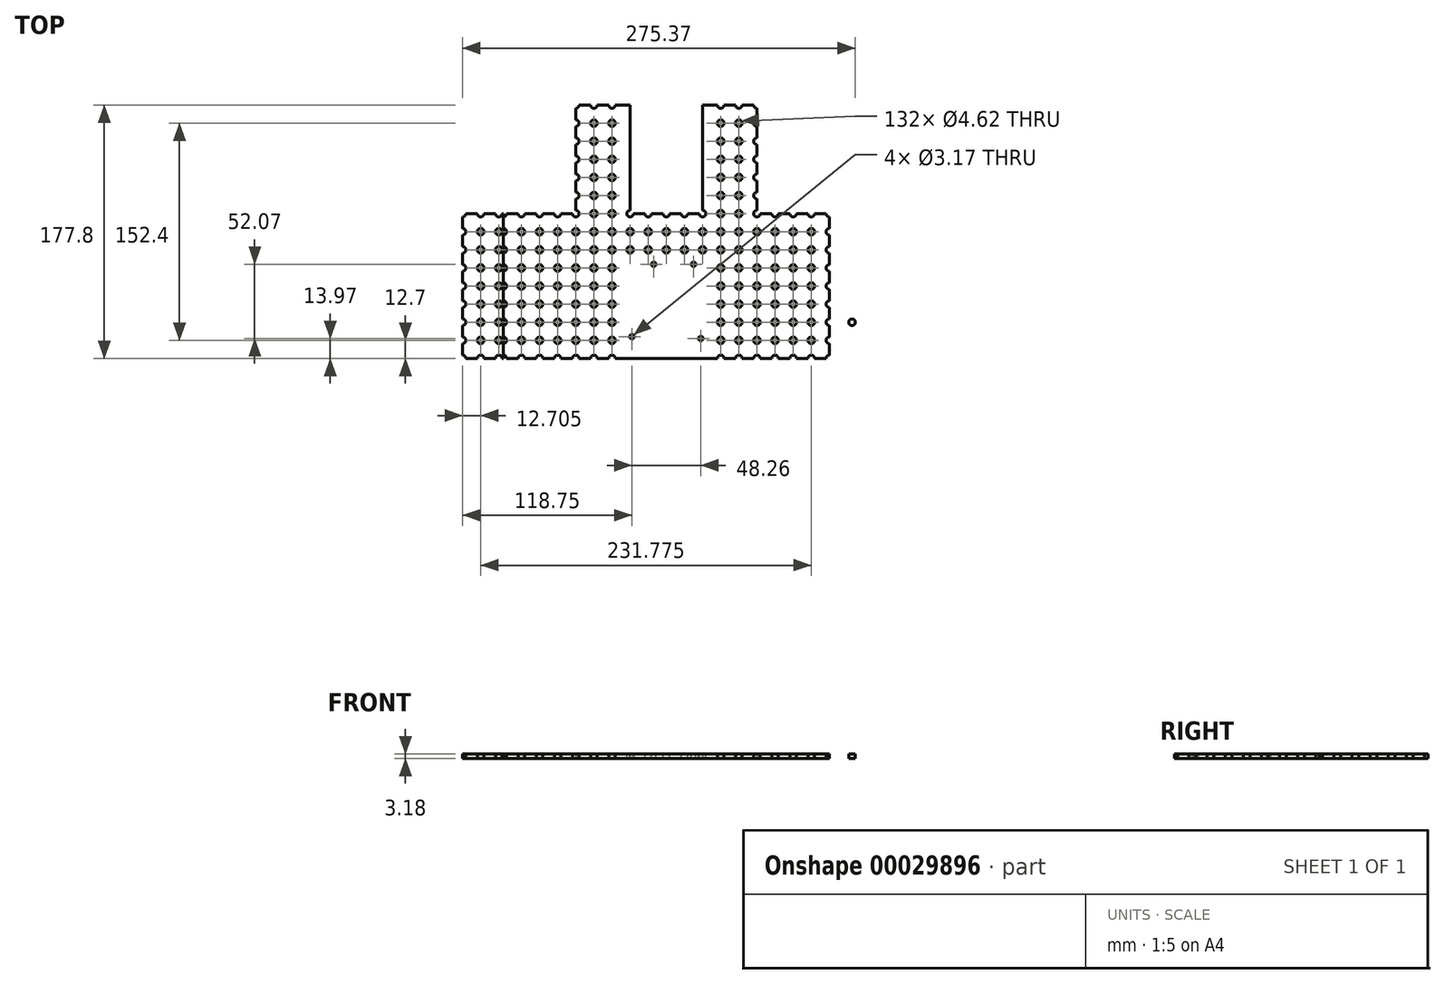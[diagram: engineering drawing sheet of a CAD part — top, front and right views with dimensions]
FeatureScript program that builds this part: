
annotation { "Feature Type Name" : "Feature", "Feature Type Description" : "" }
export const myFeature = defineFeature(function(context is Context, id is Id, definition is map)
    precondition{}
    {
        {
            var Q0;
            Q0=qCreatedBy(makeId("Top.planeOp"),FACE);
            var sketch = newSketch(context, id + "F0", { "sketchPlane" : qUnion([Q0])});
            skLineSegment(sketch, "E0", {"start": v(0, 0) * mm, "end": v(25.4, 0) * mm});
            skLineSegment(sketch, "E1", {"start": v(25.4, 0) * mm, "end": v(25.4, 76.2) * mm});
            skLineSegment(sketch, "E2", {"start": v(25.4, 76.2) * mm, "end": v(63.5, 76.2) * mm});
            skLineSegment(sketch, "E3", {"start": v(63.5, 76.2) * mm, "end": v(63.5, 0) * mm});
            skLineSegment(sketch, "E4", {"start": v(63.5, 0) * mm, "end": v(114.3, 0) * mm});
            skLineSegment(sketch, "E5", {"start": v(114.3, 0) * mm, "end": v(114.3, -101.6) * mm});
            skLineSegment(sketch, "E6", {"start": v(114.3, -101.6) * mm, "end": v(0, -101.6) * mm});
            skLineSegment(sketch, "E7", {"start": v(0, 0) * mm, "end": v(0, -101.6) * mm, "construction": true});
            skLineSegment(sketch, "E8.MirrorCS", {"start": v(0, 0) * mm, "end": v(-25.4, 0) * mm});
            skLineSegment(sketch, "E9.MirrorCS", {"start": v(-25.4, 0) * mm, "end": v(-25.4, 76.2) * mm});
            skLineSegment(sketch, "E10.MirrorCS", {"start": v(-114.3, 0) * mm, "end": v(-114.3, -101.6) * mm});
            skLineSegment(sketch, "E11.MirrorCS", {"start": v(-25.4, 76.2) * mm, "end": v(-63.5, 76.2) * mm});
            skLineSegment(sketch, "E12.MirrorCS", {"start": v(-63.5, 0) * mm, "end": v(-114.3, 0) * mm});
            skLineSegment(sketch, "E13.MirrorCS", {"start": v(-114.3, -101.6) * mm, "end": v(0, -101.6) * mm});
            skLineSegment(sketch, "E14.MirrorCS", {"start": v(-63.5, 76.2) * mm, "end": v(-63.5, 0) * mm});
            skSolve(sketch);
        }
        {
            var Q0;
            Q0=makeQuery(id+"F0.imprint","IMPRINT",FACE,{"disambiguationData":[TD([[makeQuery(id+"F0.imprint","IMPRINT",EDGE,{"derivedFrom":sQuery(id+"F0.wireOp",EDGE,"E0")}),-1.0]])]});
            extrude(context, id + "F1", {"entities" : qUnion([Q0]), "depth" : 3.17 * mm});
        }
        {
            var Q0;
            Q0=qCreatedBy(makeId("Top.planeOp"),FACE);
            var sketch = newSketch(context, id + "F2", { "sketchPlane" : qUnion([Q0])});
            skPoint(sketch, "E15.0", {"position": v(114.3, -101.6) * mm});
            skCircle(sketch, "E16", {"center": v(114.3, -101.6) * mm, "radius": 2.31 * mm});
            skCircle(sketch, "E17.0.1.0", {"center": v(114.3, -88.9) * mm, "radius": 2.31 * mm});
            skCircle(sketch, "E17.0.2.0", {"center": v(114.3, -76.2) * mm, "radius": 2.31 * mm});
            skCircle(sketch, "E17.0.3.0", {"center": v(114.3, -63.5) * mm, "radius": 2.31 * mm});
            skCircle(sketch, "E17.0.4.0", {"center": v(114.3, -50.8) * mm, "radius": 2.31 * mm});
            skCircle(sketch, "E17.0.5.0", {"center": v(114.3, -38.1) * mm, "radius": 2.31 * mm});
            skCircle(sketch, "E17.0.6.0", {"center": v(114.3, -25.4) * mm, "radius": 2.31 * mm});
            skCircle(sketch, "E17.0.7.0", {"center": v(114.3, -12.7) * mm, "radius": 2.31 * mm});
            skCircle(sketch, "E17.0.8.0", {"center": v(114.3, 0) * mm, "radius": 2.31 * mm});
            skCircle(sketch, "E17.0.9.0", {"center": v(114.3, 12.7) * mm, "radius": 2.31 * mm});
            skCircle(sketch, "E17.0.10.0", {"center": v(114.3, 25.4) * mm, "radius": 2.31 * mm});
            skCircle(sketch, "E17.0.11.0", {"center": v(114.3, 38.1) * mm, "radius": 2.31 * mm});
            skCircle(sketch, "E17.0.12.0", {"center": v(114.3, 50.8) * mm, "radius": 2.31 * mm});
            skCircle(sketch, "E17.0.13.0", {"center": v(114.3, 63.5) * mm, "radius": 2.31 * mm});
            skCircle(sketch, "E17.0.14.0", {"center": v(114.3, 76.2) * mm, "radius": 2.31 * mm});
            skCircle(sketch, "E17.1.0.0", {"center": v(101.6, -101.6) * mm, "radius": 2.31 * mm});
            skCircle(sketch, "E17.1.1.0", {"center": v(101.6, -88.9) * mm, "radius": 2.31 * mm});
            skCircle(sketch, "E17.1.2.0", {"center": v(101.6, -76.2) * mm, "radius": 2.31 * mm});
            skCircle(sketch, "E17.1.3.0", {"center": v(101.6, -63.5) * mm, "radius": 2.31 * mm});
            skCircle(sketch, "E17.1.4.0", {"center": v(101.6, -50.8) * mm, "radius": 2.31 * mm});
            skCircle(sketch, "E17.1.5.0", {"center": v(101.6, -38.1) * mm, "radius": 2.31 * mm});
            skCircle(sketch, "E17.1.6.0", {"center": v(101.6, -25.4) * mm, "radius": 2.31 * mm});
            skCircle(sketch, "E17.1.7.0", {"center": v(101.6, -12.7) * mm, "radius": 2.31 * mm});
            skCircle(sketch, "E17.1.8.0", {"center": v(101.6, 0) * mm, "radius": 2.31 * mm});
            skCircle(sketch, "E17.1.9.0", {"center": v(101.6, 12.7) * mm, "radius": 2.31 * mm});
            skCircle(sketch, "E17.1.10.0", {"center": v(101.6, 25.4) * mm, "radius": 2.31 * mm});
            skCircle(sketch, "E17.1.11.0", {"center": v(101.6, 38.1) * mm, "radius": 2.31 * mm});
            skCircle(sketch, "E17.1.12.0", {"center": v(101.6, 50.8) * mm, "radius": 2.31 * mm});
            skCircle(sketch, "E17.1.13.0", {"center": v(101.6, 63.5) * mm, "radius": 2.31 * mm});
            skCircle(sketch, "E17.1.14.0", {"center": v(101.6, 76.2) * mm, "radius": 2.31 * mm});
            skCircle(sketch, "E17.2.0.0", {"center": v(88.9, -101.6) * mm, "radius": 2.31 * mm});
            skCircle(sketch, "E17.2.1.0", {"center": v(88.9, -88.9) * mm, "radius": 2.31 * mm});
            skCircle(sketch, "E17.2.2.0", {"center": v(88.9, -76.2) * mm, "radius": 2.31 * mm});
            skCircle(sketch, "E17.2.3.0", {"center": v(88.9, -63.5) * mm, "radius": 2.31 * mm});
            skCircle(sketch, "E17.2.4.0", {"center": v(88.9, -50.8) * mm, "radius": 2.31 * mm});
            skCircle(sketch, "E17.2.5.0", {"center": v(88.9, -38.1) * mm, "radius": 2.31 * mm});
            skCircle(sketch, "E17.2.6.0", {"center": v(88.9, -25.4) * mm, "radius": 2.31 * mm});
            skCircle(sketch, "E17.2.7.0", {"center": v(88.9, -12.7) * mm, "radius": 2.31 * mm});
            skCircle(sketch, "E17.2.8.0", {"center": v(88.9, 0) * mm, "radius": 2.31 * mm});
            skCircle(sketch, "E17.2.9.0", {"center": v(88.9, 12.7) * mm, "radius": 2.31 * mm});
            skCircle(sketch, "E17.2.10.0", {"center": v(88.9, 25.4) * mm, "radius": 2.31 * mm});
            skCircle(sketch, "E17.2.11.0", {"center": v(88.9, 38.1) * mm, "radius": 2.31 * mm});
            skCircle(sketch, "E17.2.12.0", {"center": v(88.9, 50.8) * mm, "radius": 2.31 * mm});
            skCircle(sketch, "E17.2.13.0", {"center": v(88.9, 63.5) * mm, "radius": 2.31 * mm});
            skCircle(sketch, "E17.2.14.0", {"center": v(88.9, 76.2) * mm, "radius": 2.31 * mm});
            skCircle(sketch, "E17.3.0.0", {"center": v(76.2, -101.6) * mm, "radius": 2.31 * mm});
            skCircle(sketch, "E17.3.1.0", {"center": v(76.2, -88.9) * mm, "radius": 2.31 * mm});
            skCircle(sketch, "E17.3.2.0", {"center": v(76.2, -76.2) * mm, "radius": 2.31 * mm});
            skCircle(sketch, "E17.3.3.0", {"center": v(76.2, -63.5) * mm, "radius": 2.31 * mm});
            skCircle(sketch, "E17.3.4.0", {"center": v(76.2, -50.8) * mm, "radius": 2.31 * mm});
            skCircle(sketch, "E17.3.5.0", {"center": v(76.2, -38.1) * mm, "radius": 2.31 * mm});
            skCircle(sketch, "E17.3.6.0", {"center": v(76.2, -25.4) * mm, "radius": 2.31 * mm});
            skCircle(sketch, "E17.3.7.0", {"center": v(76.2, -12.7) * mm, "radius": 2.31 * mm});
            skCircle(sketch, "E17.3.8.0", {"center": v(76.2, 0) * mm, "radius": 2.31 * mm});
            skCircle(sketch, "E17.3.9.0", {"center": v(76.2, 12.7) * mm, "radius": 2.31 * mm});
            skCircle(sketch, "E17.3.10.0", {"center": v(76.2, 25.4) * mm, "radius": 2.31 * mm});
            skCircle(sketch, "E17.3.11.0", {"center": v(76.2, 38.1) * mm, "radius": 2.31 * mm});
            skCircle(sketch, "E17.3.12.0", {"center": v(76.2, 50.8) * mm, "radius": 2.31 * mm});
            skCircle(sketch, "E17.3.13.0", {"center": v(76.2, 63.5) * mm, "radius": 2.31 * mm});
            skCircle(sketch, "E17.3.14.0", {"center": v(76.2, 76.2) * mm, "radius": 2.31 * mm});
            skCircle(sketch, "E17.4.0.0", {"center": v(63.5, -101.6) * mm, "radius": 2.31 * mm});
            skCircle(sketch, "E17.4.1.0", {"center": v(63.5, -88.9) * mm, "radius": 2.31 * mm});
            skCircle(sketch, "E17.4.2.0", {"center": v(63.5, -76.2) * mm, "radius": 2.31 * mm});
            skCircle(sketch, "E17.4.3.0", {"center": v(63.5, -63.5) * mm, "radius": 2.31 * mm});
            skCircle(sketch, "E17.4.4.0", {"center": v(63.5, -50.8) * mm, "radius": 2.31 * mm});
            skCircle(sketch, "E17.4.5.0", {"center": v(63.5, -38.1) * mm, "radius": 2.31 * mm});
            skCircle(sketch, "E17.4.6.0", {"center": v(63.5, -25.4) * mm, "radius": 2.31 * mm});
            skCircle(sketch, "E17.4.7.0", {"center": v(63.5, -12.7) * mm, "radius": 2.31 * mm});
            skCircle(sketch, "E17.4.8.0", {"center": v(63.5, 0) * mm, "radius": 2.31 * mm});
            skCircle(sketch, "E17.4.9.0", {"center": v(63.5, 12.7) * mm, "radius": 2.31 * mm});
            skCircle(sketch, "E17.4.10.0", {"center": v(63.5, 25.4) * mm, "radius": 2.31 * mm});
            skCircle(sketch, "E17.4.11.0", {"center": v(63.5, 38.1) * mm, "radius": 2.31 * mm});
            skCircle(sketch, "E17.4.12.0", {"center": v(63.5, 50.8) * mm, "radius": 2.31 * mm});
            skCircle(sketch, "E17.4.13.0", {"center": v(63.5, 63.5) * mm, "radius": 2.31 * mm});
            skCircle(sketch, "E17.4.14.0", {"center": v(63.5, 76.2) * mm, "radius": 2.31 * mm});
            skLineSegment(sketch, "E17.direction1", {"start": v(114.3, -101.6) * mm, "end": v(101.6, -101.6) * mm, "construction": true});
            skLineSegment(sketch, "E17.direction2", {"start": v(114.3, -101.6) * mm, "end": v(114.3, -88.9) * mm, "construction": true});
            skLineSegment(sketch, "E18", {"start": v(0, 0) * mm, "end": v(0, -13.36) * mm, "construction": true});
            skCircle(sketch, "E19.0.5.0", {"center": v(50.8, -101.6) * mm, "radius": 2.31 * mm});
            skCircle(sketch, "E19.0.5.1", {"center": v(50.8, -88.9) * mm, "radius": 2.31 * mm});
            skCircle(sketch, "E19.0.5.2", {"center": v(50.8, -76.2) * mm, "radius": 2.31 * mm});
            skCircle(sketch, "E19.0.5.3", {"center": v(50.8, -63.5) * mm, "radius": 2.31 * mm});
            skCircle(sketch, "E19.0.5.4", {"center": v(50.8, -50.8) * mm, "radius": 2.31 * mm});
            skCircle(sketch, "E19.0.5.5", {"center": v(50.8, -38.1) * mm, "radius": 2.31 * mm});
            skCircle(sketch, "E19.0.5.6", {"center": v(50.8, -25.4) * mm, "radius": 2.31 * mm});
            skCircle(sketch, "E19.0.5.7", {"center": v(50.8, -12.7) * mm, "radius": 2.31 * mm});
            skCircle(sketch, "E19.0.5.8", {"center": v(50.8, 0) * mm, "radius": 2.31 * mm});
            skCircle(sketch, "E19.0.5.9", {"center": v(50.8, 12.7) * mm, "radius": 2.31 * mm});
            skCircle(sketch, "E19.0.5.10", {"center": v(50.8, 25.4) * mm, "radius": 2.31 * mm});
            skCircle(sketch, "E19.0.5.11", {"center": v(50.8, 38.1) * mm, "radius": 2.31 * mm});
            skCircle(sketch, "E19.0.5.12", {"center": v(50.8, 50.8) * mm, "radius": 2.31 * mm});
            skCircle(sketch, "E19.0.5.13", {"center": v(50.8, 63.5) * mm, "radius": 2.31 * mm});
            skCircle(sketch, "E19.0.5.14", {"center": v(50.8, 76.2) * mm, "radius": 2.31 * mm});
            skCircle(sketch, "E19.0.6.0", {"center": v(38.1, -101.6) * mm, "radius": 2.31 * mm});
            skCircle(sketch, "E19.0.6.1", {"center": v(38.1, -88.9) * mm, "radius": 2.31 * mm});
            skCircle(sketch, "E19.0.6.2", {"center": v(38.1, -76.2) * mm, "radius": 2.31 * mm});
            skCircle(sketch, "E19.0.6.3", {"center": v(38.1, -63.5) * mm, "radius": 2.31 * mm});
            skCircle(sketch, "E19.0.6.4", {"center": v(38.1, -50.8) * mm, "radius": 2.31 * mm});
            skCircle(sketch, "E19.0.6.5", {"center": v(38.1, -38.1) * mm, "radius": 2.31 * mm});
            skCircle(sketch, "E19.0.6.6", {"center": v(38.1, -25.4) * mm, "radius": 2.31 * mm});
            skCircle(sketch, "E19.0.6.7", {"center": v(38.1, -12.7) * mm, "radius": 2.31 * mm});
            skCircle(sketch, "E19.0.6.8", {"center": v(38.1, 0) * mm, "radius": 2.31 * mm});
            skCircle(sketch, "E19.0.6.9", {"center": v(38.1, 12.7) * mm, "radius": 2.31 * mm});
            skCircle(sketch, "E19.0.6.10", {"center": v(38.1, 25.4) * mm, "radius": 2.31 * mm});
            skCircle(sketch, "E19.0.6.11", {"center": v(38.1, 38.1) * mm, "radius": 2.31 * mm});
            skCircle(sketch, "E19.0.6.12", {"center": v(38.1, 50.8) * mm, "radius": 2.31 * mm});
            skCircle(sketch, "E19.0.6.13", {"center": v(38.1, 63.5) * mm, "radius": 2.31 * mm});
            skCircle(sketch, "E19.0.6.14", {"center": v(38.1, 76.2) * mm, "radius": 2.31 * mm});
            skCircle(sketch, "E20.MirrorC", {"center": v(-114.3, -101.6) * mm, "radius": 2.31 * mm});
            skCircle(sketch, "E21.MirrorC", {"center": v(-101.6, -76.2) * mm, "radius": 2.31 * mm});
            skCircle(sketch, "E22.MirrorC", {"center": v(-101.6, -88.9) * mm, "radius": 2.31 * mm});
            skCircle(sketch, "E23.MirrorC", {"center": v(-114.3, -88.9) * mm, "radius": 2.31 * mm});
            skCircle(sketch, "E24.MirrorC", {"center": v(-101.6, -101.6) * mm, "radius": 2.31 * mm});
            skLineSegment(sketch, "E25.MirrorCS", {"start": v(-114.3, -101.6) * mm, "end": v(-101.6, -101.6) * mm});
            skCircle(sketch, "E26.MirrorC", {"center": v(-88.9, -88.9) * mm, "radius": 2.31 * mm});
            skCircle(sketch, "E27.MirrorC", {"center": v(-76.2, -12.7) * mm, "radius": 2.31 * mm});
            skCircle(sketch, "E28.MirrorC", {"center": v(-63.5, 0) * mm, "radius": 2.31 * mm});
            skCircle(sketch, "E29.MirrorC", {"center": v(-50.8, -25.4) * mm, "radius": 2.31 * mm});
            skCircle(sketch, "E30.MirrorC", {"center": v(-38.1, -12.7) * mm, "radius": 2.31 * mm});
            skCircle(sketch, "E31.MirrorC", {"center": v(-101.6, -38.1) * mm, "radius": 2.31 * mm});
            skCircle(sketch, "E32.MirrorC", {"center": v(-88.9, -25.4) * mm, "radius": 2.31 * mm});
            skCircle(sketch, "E33.MirrorC", {"center": v(-114.3, 63.5) * mm, "radius": 2.31 * mm});
            skCircle(sketch, "E34.MirrorC", {"center": v(-76.2, -25.4) * mm, "radius": 2.31 * mm});
            skCircle(sketch, "E35.MirrorC", {"center": v(-63.5, -12.7) * mm, "radius": 2.31 * mm});
            skCircle(sketch, "E36.MirrorC", {"center": v(-50.8, -38.1) * mm, "radius": 2.31 * mm});
            skCircle(sketch, "E37.MirrorC", {"center": v(-38.1, -25.4) * mm, "radius": 2.31 * mm});
            skCircle(sketch, "E38.MirrorC", {"center": v(-101.6, -50.8) * mm, "radius": 2.31 * mm});
            skCircle(sketch, "E39.MirrorC", {"center": v(-88.9, -38.1) * mm, "radius": 2.31 * mm});
            skCircle(sketch, "E40.MirrorC", {"center": v(-101.6, -25.4) * mm, "radius": 2.31 * mm});
            skCircle(sketch, "E41.MirrorC", {"center": v(-88.9, -12.7) * mm, "radius": 2.31 * mm});
            skCircle(sketch, "E42.MirrorC", {"center": v(-76.2, -88.9) * mm, "radius": 2.31 * mm});
            skCircle(sketch, "E43.MirrorC", {"center": v(-76.2, -38.1) * mm, "radius": 2.31 * mm});
            skCircle(sketch, "E44.MirrorC", {"center": v(-50.8, 25.4) * mm, "radius": 2.31 * mm});
            skCircle(sketch, "E45.MirrorC", {"center": v(-63.5, -25.4) * mm, "radius": 2.31 * mm});
            skCircle(sketch, "E46.MirrorC", {"center": v(-50.8, -50.8) * mm, "radius": 2.31 * mm});
            skCircle(sketch, "E47.MirrorC", {"center": v(-38.1, -38.1) * mm, "radius": 2.31 * mm});
            skCircle(sketch, "E48.MirrorC", {"center": v(-63.5, -76.2) * mm, "radius": 2.31 * mm});
            skCircle(sketch, "E49.MirrorC", {"center": v(-101.6, -63.5) * mm, "radius": 2.31 * mm});
            skCircle(sketch, "E50.MirrorC", {"center": v(-38.1, 38.1) * mm, "radius": 2.31 * mm});
            skCircle(sketch, "E51.MirrorC", {"center": v(-88.9, -50.8) * mm, "radius": 2.31 * mm});
            skCircle(sketch, "E52.MirrorC", {"center": v(-101.6, 12.7) * mm, "radius": 2.31 * mm});
            skCircle(sketch, "E53.MirrorC", {"center": v(-88.9, 25.4) * mm, "radius": 2.31 * mm});
            skCircle(sketch, "E54.MirrorC", {"center": v(-76.2, 38.1) * mm, "radius": 2.31 * mm});
            skCircle(sketch, "E55.MirrorC", {"center": v(-63.5, 50.8) * mm, "radius": 2.31 * mm});
            skCircle(sketch, "E56.MirrorC", {"center": v(-76.2, -50.8) * mm, "radius": 2.31 * mm});
            skCircle(sketch, "E57.MirrorC", {"center": v(-63.5, -38.1) * mm, "radius": 2.31 * mm});
            skCircle(sketch, "E58.MirrorC", {"center": v(-50.8, 12.7) * mm, "radius": 2.31 * mm});
            skCircle(sketch, "E59.MirrorC", {"center": v(-50.8, -63.5) * mm, "radius": 2.31 * mm});
            skCircle(sketch, "E60.MirrorC", {"center": v(-38.1, -50.8) * mm, "radius": 2.31 * mm});
            skCircle(sketch, "E61.MirrorC", {"center": v(-38.1, 25.4) * mm, "radius": 2.31 * mm});
            skCircle(sketch, "E62.MirrorC", {"center": v(-38.1, 50.8) * mm, "radius": 2.31 * mm});
            skCircle(sketch, "E63.MirrorC", {"center": v(-88.9, -63.5) * mm, "radius": 2.31 * mm});
            skCircle(sketch, "E64.MirrorC", {"center": v(-101.6, 25.4) * mm, "radius": 2.31 * mm});
            skCircle(sketch, "E65.MirrorC", {"center": v(-50.8, -101.6) * mm, "radius": 2.31 * mm});
            skCircle(sketch, "E66.MirrorC", {"center": v(-38.1, -88.9) * mm, "radius": 2.31 * mm});
            skCircle(sketch, "E67.MirrorC", {"center": v(-114.3, 25.4) * mm, "radius": 2.31 * mm});
            skCircle(sketch, "E68.MirrorC", {"center": v(-114.3, 12.7) * mm, "radius": 2.31 * mm});
            skCircle(sketch, "E69.MirrorC", {"center": v(-114.3, 0) * mm, "radius": 2.31 * mm});
            skCircle(sketch, "E70.MirrorC", {"center": v(-114.3, -12.7) * mm, "radius": 2.31 * mm});
            skCircle(sketch, "E71.MirrorC", {"center": v(-88.9, -76.2) * mm, "radius": 2.31 * mm});
            skCircle(sketch, "E72.MirrorC", {"center": v(-114.3, -25.4) * mm, "radius": 2.31 * mm});
            skCircle(sketch, "E73.MirrorC", {"center": v(-114.3, -38.1) * mm, "radius": 2.31 * mm});
            skCircle(sketch, "E74.MirrorC", {"center": v(-114.3, -50.8) * mm, "radius": 2.31 * mm});
            skCircle(sketch, "E75.MirrorC", {"center": v(-114.3, -63.5) * mm, "radius": 2.31 * mm});
            skCircle(sketch, "E76.MirrorC", {"center": v(-114.3, -76.2) * mm, "radius": 2.31 * mm});
            skCircle(sketch, "E77.MirrorC", {"center": v(-76.2, -63.5) * mm, "radius": 2.31 * mm});
            skCircle(sketch, "E78.MirrorC", {"center": v(-63.5, -50.8) * mm, "radius": 2.31 * mm});
            skCircle(sketch, "E79.MirrorC", {"center": v(-50.8, -76.2) * mm, "radius": 2.31 * mm});
            skCircle(sketch, "E80.MirrorC", {"center": v(-114.3, 76.2) * mm, "radius": 2.31 * mm});
            skCircle(sketch, "E81.MirrorC", {"center": v(-38.1, -63.5) * mm, "radius": 2.31 * mm});
            skCircle(sketch, "E82.MirrorC", {"center": v(-101.6, 0) * mm, "radius": 2.31 * mm});
            skCircle(sketch, "E83.MirrorC", {"center": v(-76.2, 25.4) * mm, "radius": 2.31 * mm});
            skCircle(sketch, "E84.MirrorC", {"center": v(-88.9, 12.7) * mm, "radius": 2.31 * mm});
            skCircle(sketch, "E85.MirrorC", {"center": v(-88.9, -101.6) * mm, "radius": 2.31 * mm});
            skCircle(sketch, "E86.MirrorC", {"center": v(-50.8, 76.2) * mm, "radius": 2.31 * mm});
            skCircle(sketch, "E87.MirrorC", {"center": v(-101.6, 63.5) * mm, "radius": 2.31 * mm});
            skCircle(sketch, "E88.MirrorC", {"center": v(-88.9, 76.2) * mm, "radius": 2.31 * mm});
            skCircle(sketch, "E89.MirrorC", {"center": v(-63.5, -101.6) * mm, "radius": 2.31 * mm});
            skLineSegment(sketch, "E90.MirrorCS", {"start": v(-114.3, -101.6) * mm, "end": v(-114.3, -88.9) * mm});
            skCircle(sketch, "E91.MirrorC", {"center": v(-63.5, 38.1) * mm, "radius": 2.31 * mm});
            skCircle(sketch, "E92.MirrorC", {"center": v(-76.2, -101.6) * mm, "radius": 2.31 * mm});
            skCircle(sketch, "E93.MirrorC", {"center": v(-63.5, -88.9) * mm, "radius": 2.31 * mm});
            skCircle(sketch, "E94.MirrorC", {"center": v(-38.1, -101.6) * mm, "radius": 2.31 * mm});
            skCircle(sketch, "E95.MirrorC", {"center": v(-76.2, 12.7) * mm, "radius": 2.31 * mm});
            skCircle(sketch, "E96.MirrorC", {"center": v(-63.5, 25.4) * mm, "radius": 2.31 * mm});
            skCircle(sketch, "E97.MirrorC", {"center": v(-50.8, 0) * mm, "radius": 2.31 * mm});
            skCircle(sketch, "E98.MirrorC", {"center": v(-101.6, 76.2) * mm, "radius": 2.31 * mm});
            skCircle(sketch, "E99.MirrorC", {"center": v(-50.8, 63.5) * mm, "radius": 2.31 * mm});
            skCircle(sketch, "E100.MirrorC", {"center": v(-38.1, 12.7) * mm, "radius": 2.31 * mm});
            skCircle(sketch, "E101.MirrorC", {"center": v(-101.6, -12.7) * mm, "radius": 2.31 * mm});
            skCircle(sketch, "E102.MirrorC", {"center": v(-50.8, 50.8) * mm, "radius": 2.31 * mm});
            skCircle(sketch, "E103.MirrorC", {"center": v(-38.1, 63.5) * mm, "radius": 2.31 * mm});
            skCircle(sketch, "E104.MirrorC", {"center": v(-101.6, 38.1) * mm, "radius": 2.31 * mm});
            skCircle(sketch, "E105.MirrorC", {"center": v(-88.9, 50.8) * mm, "radius": 2.31 * mm});
            skCircle(sketch, "E106.MirrorC", {"center": v(-76.2, 63.5) * mm, "radius": 2.31 * mm});
            skCircle(sketch, "E107.MirrorC", {"center": v(-63.5, 76.2) * mm, "radius": 2.31 * mm});
            skCircle(sketch, "E108.MirrorC", {"center": v(-88.9, 0) * mm, "radius": 2.31 * mm});
            skCircle(sketch, "E109.MirrorC", {"center": v(-50.8, 38.1) * mm, "radius": 2.31 * mm});
            skCircle(sketch, "E110.MirrorC", {"center": v(-114.3, 50.8) * mm, "radius": 2.31 * mm});
            skCircle(sketch, "E111.MirrorC", {"center": v(-88.9, 38.1) * mm, "radius": 2.31 * mm});
            skCircle(sketch, "E112.MirrorC", {"center": v(-76.2, 50.8) * mm, "radius": 2.31 * mm});
            skCircle(sketch, "E113.MirrorC", {"center": v(-114.3, 38.1) * mm, "radius": 2.31 * mm});
            skCircle(sketch, "E114.MirrorC", {"center": v(-63.5, 63.5) * mm, "radius": 2.31 * mm});
            skCircle(sketch, "E115.MirrorC", {"center": v(-38.1, 76.2) * mm, "radius": 2.31 * mm});
            skCircle(sketch, "E116.MirrorC", {"center": v(-101.6, 50.8) * mm, "radius": 2.31 * mm});
            skCircle(sketch, "E117.MirrorC", {"center": v(-88.9, 63.5) * mm, "radius": 2.31 * mm});
            skCircle(sketch, "E118.MirrorC", {"center": v(-76.2, 76.2) * mm, "radius": 2.31 * mm});
            skCircle(sketch, "E119.MirrorC", {"center": v(-76.2, 0) * mm, "radius": 2.31 * mm});
            skCircle(sketch, "E120.MirrorC", {"center": v(-63.5, 12.7) * mm, "radius": 2.31 * mm});
            skCircle(sketch, "E121.MirrorC", {"center": v(-76.2, -76.2) * mm, "radius": 2.31 * mm});
            skCircle(sketch, "E122.MirrorC", {"center": v(-50.8, -12.7) * mm, "radius": 2.31 * mm});
            skCircle(sketch, "E123.MirrorC", {"center": v(-38.1, 0) * mm, "radius": 2.31 * mm});
            skCircle(sketch, "E124.MirrorC", {"center": v(-63.5, -63.5) * mm, "radius": 2.31 * mm});
            skCircle(sketch, "E125.MirrorC", {"center": v(-50.8, -88.9) * mm, "radius": 2.31 * mm});
            skCircle(sketch, "E126.MirrorC", {"center": v(-38.1, -76.2) * mm, "radius": 2.31 * mm});
            skSolve(sketch);
        }
        {
            var Q0;
            Q0 = qSketchRegion(id + "F2", true);
            extrude(context, id + "F3", {"entities" : qUnion([Q0]), "operationType" : NewBodyOperationType.REMOVE, "endBound" : BoundingType.THROUGH_ALL, "depth" : 25.4 * mm});
        }
        {
            var Q0;
            Q0=makeQuery(id+"F1.opExtrude","CAP_FACE",FACE,{"disambiguationData":[OSD([sQuery(id+"F0.wireOp",EDGE,"E0"),sQuery(id+"F0.wireOp",EDGE,"E1"),sQuery(id+"F0.wireOp",EDGE,"E2"),sQuery(id+"F0.wireOp",EDGE,"E3"),sQuery(id+"F0.wireOp",EDGE,"E4"),sQuery(id+"F0.wireOp",EDGE,"E5"),sQuery(id+"F0.wireOp",EDGE,"E6"),sQuery(id+"F0.wireOp",EDGE,"E8.MirrorCS"),sQuery(id+"F0.wireOp",EDGE,"E9.MirrorCS"),sQuery(id+"F0.wireOp",EDGE,"E10.MirrorCS"),sQuery(id+"F0.wireOp",EDGE,"E11.MirrorCS"),sQuery(id+"F0.wireOp",EDGE,"E12.MirrorCS"),sQuery(id+"F0.wireOp",EDGE,"E13.MirrorCS"),sQuery(id+"F0.wireOp",EDGE,"E14.MirrorCS")])],"isStart":false});
            var sketch = newSketch(context, id + "F4", { "sketchPlane" : qUnion([Q0])});
            skCircle(sketch, "E127", {"center": v(-24.13, -86.36) * mm, "radius": 1.59 * mm});
            skCircle(sketch, "E128", {"center": v(24.13, -87.63) * mm, "radius": 1.59 * mm});
            skCircle(sketch, "E129", {"center": v(-8.9, -35.56) * mm, "radius": 1.59 * mm});
            skCircle(sketch, "E130", {"center": v(19.05, -35.56) * mm, "radius": 1.59 * mm});
            skLineSegment(sketch, "E131", {"start": v(0, 0) * mm, "end": v(0, -101.6) * mm, "construction": true});
            skCircle(sketch, "E132", {"center": v(25.4, -25.4) * mm, "radius": 2.31 * mm});
            skCircle(sketch, "E133.0", {"center": v(63.5, -25.4) * mm, "radius": 2.31 * mm});
            skCircle(sketch, "E134.0.1.0", {"center": v(25.4, -12.7) * mm, "radius": 2.31 * mm});
            skCircle(sketch, "E134.0.2.0", {"center": v(25.4, 0) * mm, "radius": 2.31 * mm});
            skCircle(sketch, "E134.1.0.0", {"center": v(12.7, -25.4) * mm, "radius": 2.31 * mm});
            skCircle(sketch, "E134.1.1.0", {"center": v(12.7, -12.7) * mm, "radius": 2.31 * mm});
            skCircle(sketch, "E134.1.2.0", {"center": v(12.7, 0) * mm, "radius": 2.31 * mm});
            skCircle(sketch, "E134.2.0.0", {"center": v(0, -25.4) * mm, "radius": 2.31 * mm});
            skCircle(sketch, "E134.2.1.0", {"center": v(0, -12.7) * mm, "radius": 2.31 * mm});
            skCircle(sketch, "E134.2.2.0", {"center": v(0, 0) * mm, "radius": 2.31 * mm});
            skCircle(sketch, "E134.3.0.0", {"center": v(-12.7, -25.4) * mm, "radius": 2.31 * mm});
            skCircle(sketch, "E134.3.1.0", {"center": v(-12.7, -12.7) * mm, "radius": 2.31 * mm});
            skCircle(sketch, "E134.3.2.0", {"center": v(-12.7, 0) * mm, "radius": 2.31 * mm});
            skCircle(sketch, "E134.4.0.0", {"center": v(-25.4, -25.4) * mm, "radius": 2.31 * mm});
            skCircle(sketch, "E134.4.1.0", {"center": v(-25.4, -12.7) * mm, "radius": 2.31 * mm});
            skCircle(sketch, "E134.4.2.0", {"center": v(-25.4, 0) * mm, "radius": 2.31 * mm});
            skLineSegment(sketch, "E134.direction1", {"start": v(25.4, -25.4) * mm, "end": v(12.7, -25.4) * mm, "construction": true});
            skLineSegment(sketch, "E134.direction2", {"start": v(25.4, -25.4) * mm, "end": v(25.4, -12.7) * mm, "construction": true});
            skSolve(sketch);
        }
        {
            var Q0;
            Q0 = qSketchRegion(id + "F4", true);
            extrude(context, id + "F5", {"entities" : qUnion([Q0]), "operationType" : NewBodyOperationType.REMOVE, "oppositeDirection" : true, "depth" : 25.4 * mm});
        }
        {
            var Q0;
            Q0=qCreatedBy(makeId("Top.planeOp"),FACE);
            var sketch = newSketch(context, id + "F6", { "sketchPlane" : qUnion([Q0])});
            skLineSegment(sketch, "E135.0", {"start": v(-114.3, -91.21) * mm, "end": v(-114.3, -99.29) * mm, "construction": true});
            skLineSegment(sketch, "E136.0", {"start": v(-103.91, 0) * mm, "end": v(-111.99, 0) * mm, "construction": true});
            skLineSegment(sketch, "E137.0", {"start": v(103.91, -101.6) * mm, "end": v(111.99, -101.6) * mm, "construction": true});
            skLineSegment(sketch, "E138.bottom", {"start": v(-114.3, 0) * mm, "end": v(-142.88, 0) * mm});
            skLineSegment(sketch, "E138.top", {"start": v(-114.3, -101.6) * mm, "end": v(-142.88, -101.6) * mm});
            skLineSegment(sketch, "E138.left", {"start": v(-114.3, 0) * mm, "end": v(-114.3, -101.6) * mm});
            skLineSegment(sketch, "E138.right", {"start": v(-142.88, 0) * mm, "end": v(-142.88, -101.6) * mm});
            skCircle(sketch, "E139", {"center": v(-142.88, -101.6) * mm, "radius": 2.31 * mm});
            skCircle(sketch, "E140.0.1.0", {"center": v(-142.88, -88.9) * mm, "radius": 2.31 * mm});
            skCircle(sketch, "E140.0.2.0", {"center": v(-142.88, -76.2) * mm, "radius": 2.31 * mm});
            skCircle(sketch, "E140.0.3.0", {"center": v(-142.88, -63.5) * mm, "radius": 2.31 * mm});
            skCircle(sketch, "E140.0.4.0", {"center": v(-142.88, -50.8) * mm, "radius": 2.31 * mm});
            skCircle(sketch, "E140.0.5.0", {"center": v(-142.88, -38.1) * mm, "radius": 2.31 * mm});
            skCircle(sketch, "E140.0.6.0", {"center": v(-142.88, -25.4) * mm, "radius": 2.31 * mm});
            skCircle(sketch, "E140.0.7.0", {"center": v(-142.88, -12.7) * mm, "radius": 2.31 * mm});
            skCircle(sketch, "E140.0.8.0", {"center": v(-142.88, 0) * mm, "radius": 2.31 * mm});
            skCircle(sketch, "E140.1.0.0", {"center": v(-130.18, -101.6) * mm, "radius": 2.31 * mm});
            skCircle(sketch, "E140.1.1.0", {"center": v(-130.18, -88.9) * mm, "radius": 2.31 * mm});
            skCircle(sketch, "E140.1.2.0", {"center": v(-130.18, -76.2) * mm, "radius": 2.31 * mm});
            skCircle(sketch, "E140.1.3.0", {"center": v(-130.18, -63.5) * mm, "radius": 2.31 * mm});
            skCircle(sketch, "E140.1.4.0", {"center": v(-130.18, -50.8) * mm, "radius": 2.31 * mm});
            skCircle(sketch, "E140.1.5.0", {"center": v(-130.18, -38.1) * mm, "radius": 2.31 * mm});
            skCircle(sketch, "E140.1.6.0", {"center": v(-130.18, -25.4) * mm, "radius": 2.31 * mm});
            skCircle(sketch, "E140.1.7.0", {"center": v(-130.18, -12.7) * mm, "radius": 2.31 * mm});
            skCircle(sketch, "E140.1.8.0", {"center": v(-130.18, 0) * mm, "radius": 2.31 * mm});
            skCircle(sketch, "E140.2.0.0", {"center": v(-117.48, -101.6) * mm, "radius": 2.31 * mm});
            skCircle(sketch, "E140.2.1.0", {"center": v(-117.48, -88.9) * mm, "radius": 2.31 * mm});
            skCircle(sketch, "E140.2.2.0", {"center": v(-117.48, -76.2) * mm, "radius": 2.31 * mm});
            skCircle(sketch, "E140.2.3.0", {"center": v(-117.48, -63.5) * mm, "radius": 2.31 * mm});
            skCircle(sketch, "E140.2.4.0", {"center": v(-117.48, -50.8) * mm, "radius": 2.31 * mm});
            skCircle(sketch, "E140.2.5.0", {"center": v(-117.48, -38.1) * mm, "radius": 2.31 * mm});
            skCircle(sketch, "E140.2.6.0", {"center": v(-117.48, -25.4) * mm, "radius": 2.31 * mm});
            skCircle(sketch, "E140.2.7.0", {"center": v(-117.48, -12.7) * mm, "radius": 2.31 * mm});
            skCircle(sketch, "E140.2.8.0", {"center": v(-117.48, 0) * mm, "radius": 2.31 * mm});
            skLineSegment(sketch, "E140.direction1", {"start": v(-142.88, -101.6) * mm, "end": v(-130.18, -101.6) * mm, "construction": true});
            skLineSegment(sketch, "E140.direction2", {"start": v(-142.88, -101.6) * mm, "end": v(-142.88, -88.9) * mm, "construction": true});
            skCircle(sketch, "E141.MirrorC", {"center": v(142.88, -101.6) * mm, "radius": 2.31 * mm});
            skCircle(sketch, "E142.MirrorC", {"center": v(142.88, 0) * mm, "radius": 2.31 * mm});
            skCircle(sketch, "E143.MirrorC", {"center": v(130.18, -101.6) * mm, "radius": 2.31 * mm});
            skCircle(sketch, "E144.MirrorC", {"center": v(142.88, -88.9) * mm, "radius": 2.31 * mm});
            skCircle(sketch, "E145.MirrorC", {"center": v(142.88, -12.7) * mm, "radius": 2.31 * mm});
            skCircle(sketch, "E146.MirrorC", {"center": v(142.88, -25.4) * mm, "radius": 2.31 * mm});
            skCircle(sketch, "E147.MirrorC", {"center": v(142.88, -38.1) * mm, "radius": 2.31 * mm});
            skCircle(sketch, "E148.MirrorC", {"center": v(130.18, -76.2) * mm, "radius": 2.31 * mm});
            skLineSegment(sketch, "E149.MirrorCS", {"start": v(142.88, -101.6) * mm, "end": v(130.18, -101.6) * mm});
            skCircle(sketch, "E150.MirrorC", {"center": v(117.48, -101.6) * mm, "radius": 2.31 * mm});
            skCircle(sketch, "E151.MirrorC", {"center": v(130.18, -88.9) * mm, "radius": 2.31 * mm});
            skCircle(sketch, "E152.MirrorC", {"center": v(117.48, 0) * mm, "radius": 2.31 * mm});
            skCircle(sketch, "E153.MirrorC", {"center": v(130.18, -38.1) * mm, "radius": 2.31 * mm});
            skCircle(sketch, "E154.MirrorC", {"center": v(117.48, -38.1) * mm, "radius": 2.31 * mm});
            skCircle(sketch, "E155.MirrorC", {"center": v(130.18, 0) * mm, "radius": 2.31 * mm});
            skCircle(sketch, "E156.MirrorC", {"center": v(130.18, -12.7) * mm, "radius": 2.31 * mm});
            skCircle(sketch, "E157.MirrorC", {"center": v(130.18, -50.8) * mm, "radius": 2.31 * mm});
            skCircle(sketch, "E158.MirrorC", {"center": v(117.48, -50.8) * mm, "radius": 2.31 * mm});
            skCircle(sketch, "E159.MirrorC", {"center": v(117.48, -76.2) * mm, "radius": 2.31 * mm});
            skCircle(sketch, "E160.MirrorC", {"center": v(117.48, -12.7) * mm, "radius": 2.31 * mm});
            skCircle(sketch, "E161.MirrorC", {"center": v(130.18, -25.4) * mm, "radius": 2.31 * mm});
            skCircle(sketch, "E162.MirrorC", {"center": v(130.18, -63.5) * mm, "radius": 2.31 * mm});
            skCircle(sketch, "E163.MirrorC", {"center": v(117.48, -63.5) * mm, "radius": 2.31 * mm});
            skLineSegment(sketch, "E164.MirrorCS", {"start": v(142.88, -101.6) * mm, "end": v(142.88, -88.9) * mm});
            skCircle(sketch, "E165.MirrorC", {"center": v(142.88, -63.5) * mm, "radius": 2.31 * mm});
            skCircle(sketch, "E166.MirrorC", {"center": v(117.48, -88.9) * mm, "radius": 2.31 * mm});
            skCircle(sketch, "E167.MirrorC", {"center": v(117.48, -25.4) * mm, "radius": 2.31 * mm});
            skCircle(sketch, "E168.MirrorC", {"center": v(142.88, -50.8) * mm, "radius": 2.31 * mm});
            skCircle(sketch, "E169.MirrorC", {"center": v(142.88, -76.2) * mm, "radius": 2.31 * mm});
            skLineSegment(sketch, "E170.MirrorCS", {"start": v(142.88, 0) * mm, "end": v(142.88, -101.6) * mm});
            skLineSegment(sketch, "E171.MirrorCS", {"start": v(114.3, -101.6) * mm, "end": v(142.88, -101.6) * mm});
            skLineSegment(sketch, "E172.MirrorCS", {"start": v(114.3, 0) * mm, "end": v(142.88, 0) * mm});
            skLineSegment(sketch, "E173", {"start": v(114.3, 0) * mm, "end": v(114.3, -101.6) * mm});
            skSolve(sketch);
        }
        {
            var Q0;
            {var subQ20=sQuery(id+"F6.wireOp",EDGE,"E138.left");Q0=makeQuery(id+"F6.imprint","IMPRINT",FACE,{"disambiguationData":[TD([[makeQuery(id+"F6.imprint","IMPRINT",EDGE,{"derivedFrom":subQ20}),-1.0]])]});}
            var Q1;
            Q1=makeQuery(id+"F6.imprint","IMPRINT",FACE,{"disambiguationData":[TD([[makeQuery(id+"F6.imprint","IMPRINT",EDGE,{"derivedFrom":sQuery(id+"F6.wireOp",EDGE,"E148.MirrorC")}),1.0]])]});
            extrude(context, id + "F7", {"entities" : qUnion([Q0, Q1]), "depth" : 3.17 * mm});
        }
    });
